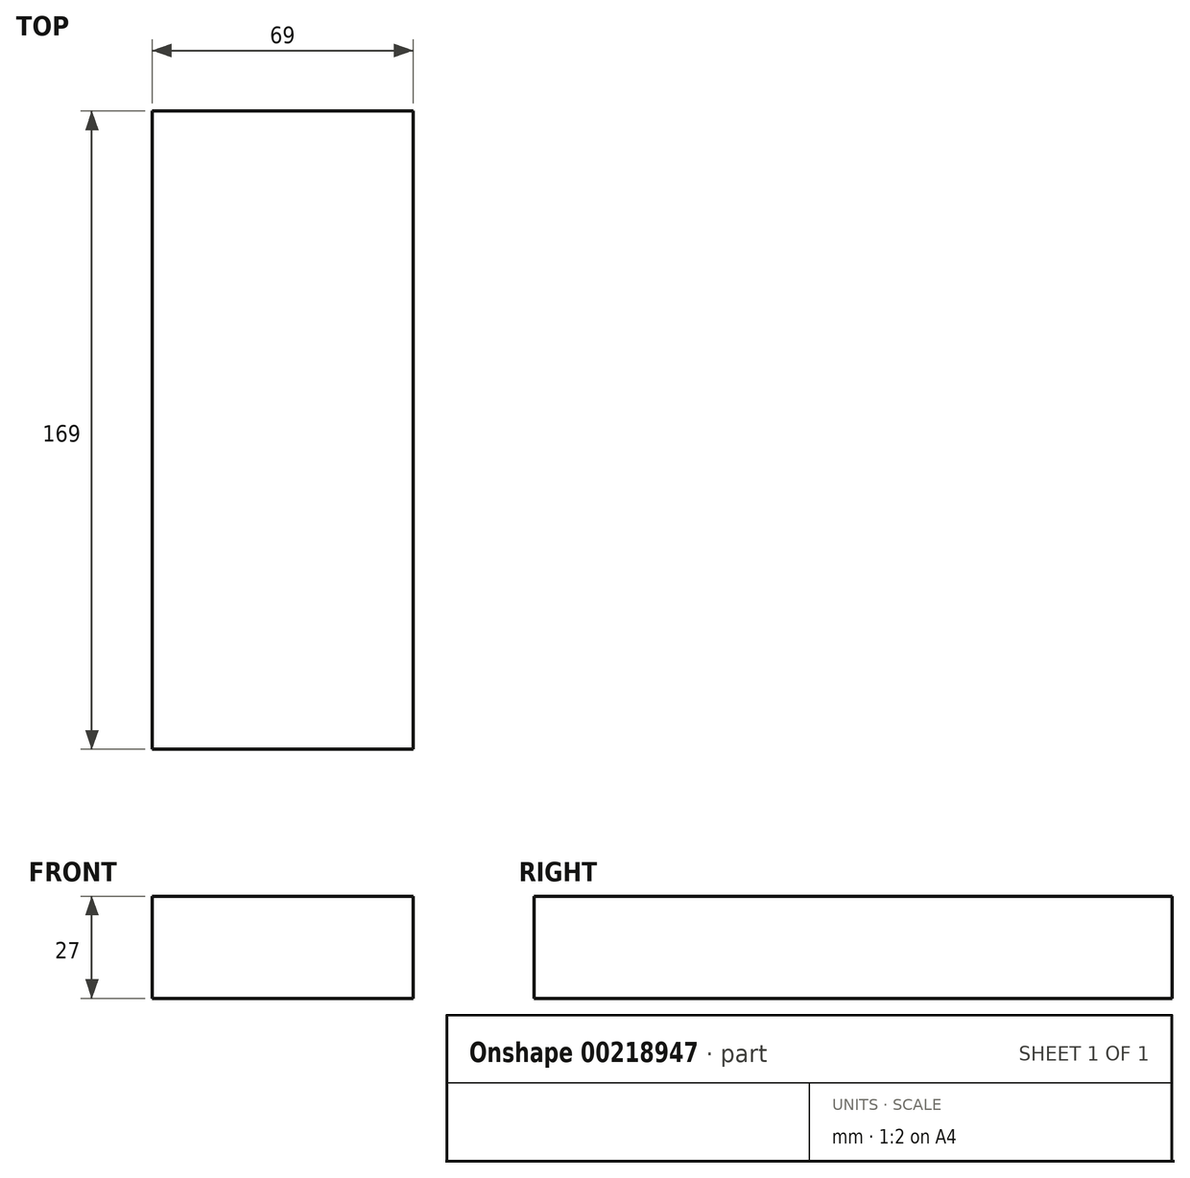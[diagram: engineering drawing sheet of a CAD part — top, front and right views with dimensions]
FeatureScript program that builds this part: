
annotation { "Feature Type Name" : "Feature", "Feature Type Description" : "" }
export const myFeature = defineFeature(function(context is Context, id is Id, definition is map)
    precondition{}
    {
        {
            var Q0;
            Q0=qCreatedBy(makeId("Top.planeOp"),FACE);
            var sketch = newSketch(context, id + "F0", { "sketchPlane" : qUnion([Q0])});
            skLineSegment(sketch, "E0.bottom", {"start": v(0, 0) * mm, "end": v(69, 0) * mm});
            skLineSegment(sketch, "E0.top", {"start": v(0, -169) * mm, "end": v(69, -169) * mm});
            skLineSegment(sketch, "E0.left", {"start": v(0, 0) * mm, "end": v(0, -169) * mm});
            skLineSegment(sketch, "E0.right", {"start": v(69, 0) * mm, "end": v(69, -169) * mm});
            skSolve(sketch);
        }
        {
            var Q0;
            Q0=makeQuery(id+"F0.imprint","IMPRINT",FACE,{"disambiguationData":[TD([[makeQuery(id+"F0.imprint","IMPRINT",EDGE,{"derivedFrom":sQuery(id+"F0.wireOp",EDGE,"E0.bottom")}),-1.0]])]});
            extrude(context, id + "F1", {"entities" : qUnion([Q0]), "depth" : 27 * mm});
        }
    });
